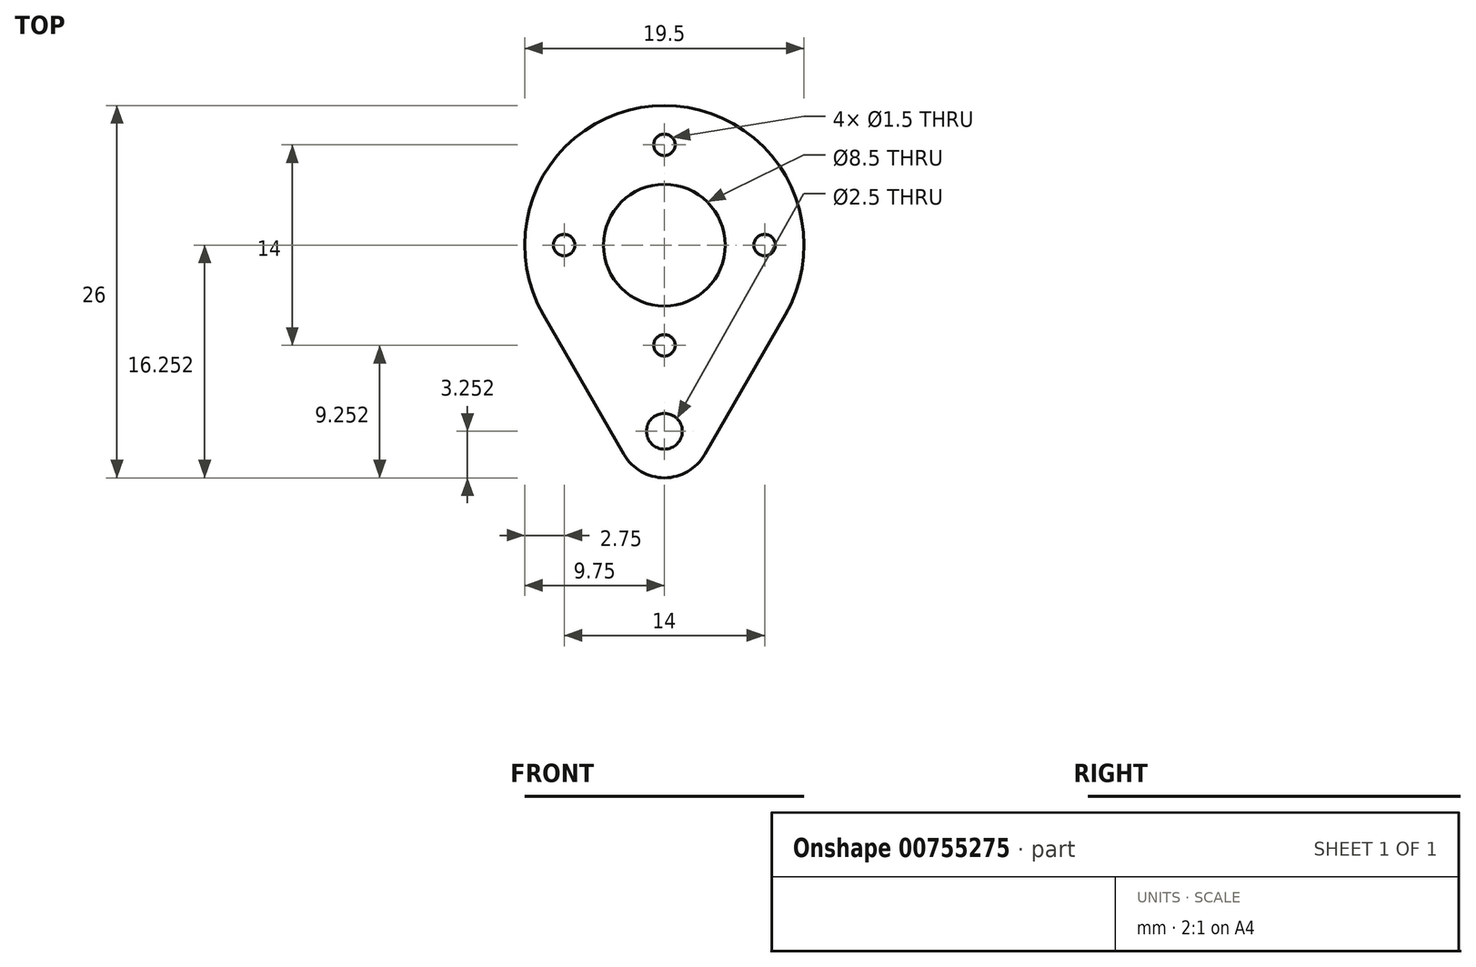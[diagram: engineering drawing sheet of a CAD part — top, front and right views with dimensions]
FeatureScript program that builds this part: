
annotation { "Feature Type Name" : "Feature", "Feature Type Description" : "" }
export const myFeature = defineFeature(function(context is Context, id is Id, definition is map)
    precondition{}
    {
        {
            var Q0;
            Q0=qCreatedBy(makeId("Top.planeOp"),FACE);
            var sketch = newSketch(context, id + "F0", { "sketchPlane" : qUnion([Q0])});
            skCircle(sketch, "E0", {"center": v(-41.31, 26.1) * mm, "radius": 0.75 * mm});
            skCircle(sketch, "E1", {"center": v(-34.31, 19.1) * mm, "radius": 0.75 * mm});
            skCircle(sketch, "E2.MirrorC", {"center": v(-48.31, 19.1) * mm, "radius": 0.75 * mm});
            skCircle(sketch, "E3.MirrorC", {"center": v(-41.31, 12.1) * mm, "radius": 0.75 * mm});
            skCircle(sketch, "E4", {"center": v(-41.31, 19.1) * mm, "radius": 4.25 * mm});
            skArc(sketch, "E5", {"start": v(-32.87, 14.23) * mm, "mid": v(-41.31, 28.85) * mm, "end": v(-49.75, 14.23) * mm});
            skCircle(sketch, "E6", {"center": v(-41.31, 6.1) * mm, "radius": 1.25 * mm});
            skArc(sketch, "E7", {"start": v(-44.12, 4.48) * mm, "mid": v(-41.31, 2.85) * mm, "end": v(-38.5, 4.48) * mm});
            skLineSegment(sketch, "E8", {"start": v(-44.12, 4.48) * mm, "end": v(-49.75, 14.23) * mm});
            skLineSegment(sketch, "E9.MirrorCS", {"start": v(-38.5, 4.48) * mm, "end": v(-32.87, 14.23) * mm});
            skSolve(sketch);
        }
        {
            var Q0;
            Q0=makeQuery(id+"F0.imprint","IMPRINT",FACE,{"disambiguationData":[TD([[makeQuery(id+"F0.imprint","IMPRINT",EDGE,{"derivedFrom":sQuery(id+"F0.wireOp",EDGE,"E0")}),-1.0]])]});
            var Q1;
            {var subQ0=sQuery(id+"F0.wireOp",EDGE,"E9.MirrorCS");Q1=makeQuery(id+"F0.imprint","IMPRINT",FACE,{"disambiguationData":[TD([[makeQuery(id+"F0.imprint","IMPRINT",EDGE,{"derivedFrom":subQ0}),1.0]])]});}
            var Q2;
            {var subQ0=sQuery(id+"F0.wireOp",EDGE,"E8");Q2=makeQuery(id+"F0.imprint","IMPRINT",FACE,{"disambiguationData":[TD([[makeQuery(id+"F0.imprint","IMPRINT",EDGE,{"derivedFrom":subQ0}),-1.0]])]});}
            var Q3;
            Q3=makeQuery(id+"F0.imprint","IMPRINT",FACE,{"disambiguationData":[TD([[makeQuery(id+"F0.imprint","IMPRINT",EDGE,{"derivedFrom":sQuery(id+"F0.wireOp",EDGE,"E6")}),-1.0]])]});
            extrude(context, id + "F1", {"entities" : qUnion([Q0, Q1, Q2, Q3]), "depth" : 1 / 203.2 * mm, "offsetDistance" : 25 * mm});
        }
    });
